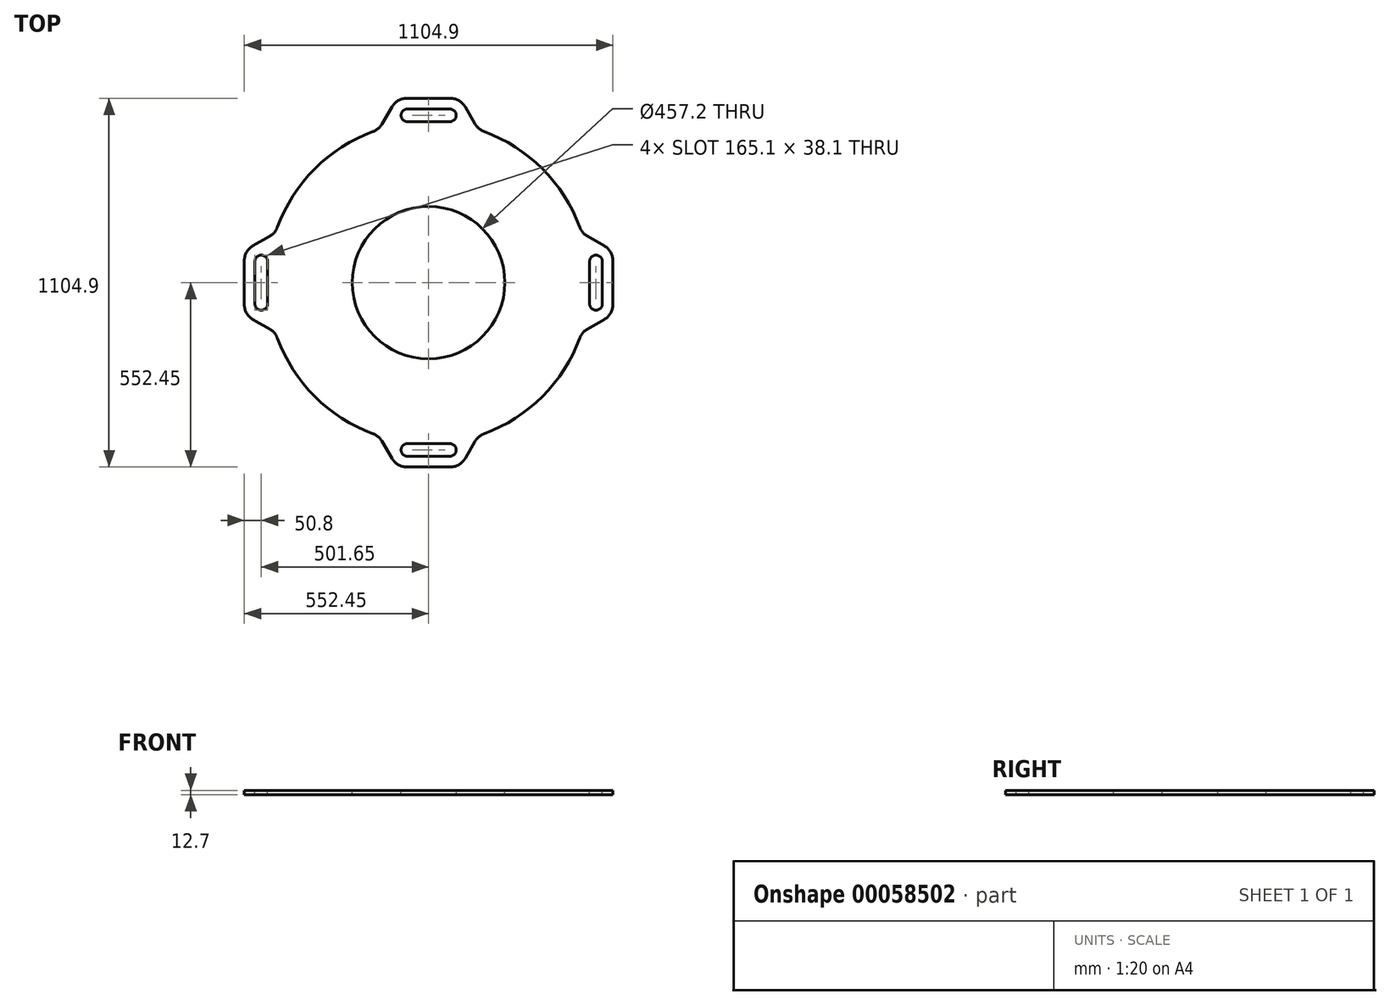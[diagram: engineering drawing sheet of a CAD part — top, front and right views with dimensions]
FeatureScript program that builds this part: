
annotation { "Feature Type Name" : "Feature", "Feature Type Description" : "" }
export const myFeature = defineFeature(function(context is Context, id is Id, definition is map)
    precondition{}
    {
        {
            var Q0;
            Q0=qCreatedBy(makeId("Top.planeOp"),FACE);
            var sketch = newSketch(context, id + "F0", { "sketchPlane" : qUnion([Q0])});
            skLineSegment(sketch, "E0.bottom", {"start": v(-552.45, 95.25) * mm, "end": v(552.45, 95.25) * mm});
            skLineSegment(sketch, "E0.top", {"start": v(-552.45, -95.25) * mm, "end": v(552.45, -95.25) * mm});
            skLineSegment(sketch, "E0.left", {"start": v(-552.45, 95.25) * mm, "end": v(-552.45, -95.25) * mm});
            skLineSegment(sketch, "E0.right", {"start": v(552.45, 95.25) * mm, "end": v(552.45, -95.25) * mm});
            skCircle(sketch, "E1", {"center": v(0, 0) * mm, "radius": 228.6 * mm});
            skCircle(sketch, "E2", {"center": v(0, 0) * mm, "radius": 482.6 * mm});
            skLineSegment(sketch, "E3.bottom", {"start": v(-95.25, 552.45) * mm, "end": v(95.25, 552.45) * mm});
            skLineSegment(sketch, "E3.top", {"start": v(-95.25, -552.45) * mm, "end": v(95.25, -552.45) * mm});
            skLineSegment(sketch, "E3.left", {"start": v(-95.25, 552.45) * mm, "end": v(-95.25, -552.45) * mm});
            skLineSegment(sketch, "E3.right", {"start": v(95.25, 552.45) * mm, "end": v(95.25, -552.45) * mm});
            skLineSegment(sketch, "E4.bottom", {"start": v(-520.7, 82.55) * mm, "end": v(-482.6, 82.55) * mm});
            skLineSegment(sketch, "E4.top", {"start": v(-520.7, -82.55) * mm, "end": v(-482.6, -82.55) * mm});
            skLineSegment(sketch, "E4.left", {"start": v(-520.7, 82.55) * mm, "end": v(-520.7, -82.55) * mm});
            skLineSegment(sketch, "E4.right", {"start": v(-482.6, 82.55) * mm, "end": v(-482.6, -82.55) * mm});
            skLineSegment(sketch, "E5", {"start": v(-552.45, 95.25) * mm, "end": v(-458.95, 149.23) * mm});
            skLineSegment(sketch, "E6", {"start": v(-552.45, -95.25) * mm, "end": v(-458.95, -149.23) * mm});
            skLineSegment(sketch, "E7", {"start": v(-95.25, 552.45) * mm, "end": v(-149.23, 458.95) * mm});
            skLineSegment(sketch, "E8", {"start": v(95.25, 552.45) * mm, "end": v(149.23, 458.95) * mm});
            skLineSegment(sketch, "E9", {"start": v(552.45, 95.25) * mm, "end": v(458.95, 149.23) * mm});
            skLineSegment(sketch, "E10", {"start": v(552.45, -95.25) * mm, "end": v(458.95, -149.23) * mm});
            skLineSegment(sketch, "E11", {"start": v(95.25, -552.45) * mm, "end": v(149.23, -458.95) * mm});
            skLineSegment(sketch, "E12", {"start": v(-95.25, -552.45) * mm, "end": v(-149.23, -458.95) * mm});
            skSolve(sketch);
        }
        {
            var Q0;
            {var subQ0=sQuery(id+"F0.wireOp",EDGE,"E0.right");Q0=makeQuery(id+"F0.imprint","IMPRINT",FACE,{"disambiguationData":[TD([[makeQuery(id+"F0.imprint","IMPRINT",EDGE,{"derivedFrom":subQ0}),-1.0]])]});}
            var Q1;
            {var subQ0=sQuery(id+"F0.wireOp",EDGE,"E2");var subQ1=sQuery(id+"F0.wireOp",EDGE,"E0.bottom");var subQ2=makeQuery(id+"F0.imprint","INTERSECT",VERTEX,{"disambiguationData":[OD(0.0)],"derivedFrom":[subQ1,subQ0]});Q1=makeQuery(id+"F0.imprint","IMPRINT",FACE,{"disambiguationData":[TD([[makeQuery(id+"F0.imprint","IMPRINT",EDGE,{"disambiguationData":[TD([[subQ2,-1.0]])],"derivedFrom":subQ1}),-1.0]])]});}
            var Q2;
            {var subQ0=sQuery(id+"F0.wireOp",EDGE,"E2");var subQ1=sQuery(id+"F0.wireOp",EDGE,"E0.bottom");var subQ2=makeQuery(id+"F0.imprint","INTERSECT",VERTEX,{"disambiguationData":[OD(1.0)],"derivedFrom":[subQ1,subQ0]});Q2=makeQuery(id+"F0.imprint","IMPRINT",FACE,{"disambiguationData":[TD([[makeQuery(id+"F0.imprint","IMPRINT",EDGE,{"disambiguationData":[TD([[subQ2,1.0]])],"derivedFrom":subQ1}),-1.0]])]});}
            var Q3;
            {var subQ0=sQuery(id+"F0.wireOp",EDGE,"E2");var subQ1=sQuery(id+"F0.wireOp",EDGE,"E0.bottom");var subQ2=makeQuery(id+"F0.imprint","INTERSECT",VERTEX,{"disambiguationData":[OD(0.0)],"derivedFrom":[subQ1,subQ0]});Q3=makeQuery(id+"F0.imprint","IMPRINT",FACE,{"disambiguationData":[TD([[makeQuery(id+"F0.imprint","IMPRINT",EDGE,{"disambiguationData":[TD([[subQ2,-1.0]])],"derivedFrom":subQ1}),1.0]])]});}
            var Q4;
            {var subQ0=sQuery(id+"F0.wireOp",EDGE,"E3.right");var subQ1=sQuery(id+"F0.wireOp",EDGE,"E1");var subQ2=makeQuery(id+"F0.imprint","INTERSECT",VERTEX,{"disambiguationData":[OD(0.0)],"derivedFrom":[subQ1,subQ0]});Q4=makeQuery(id+"F0.imprint","IMPRINT",FACE,{"disambiguationData":[TD([[makeQuery(id+"F0.imprint","IMPRINT",EDGE,{"disambiguationData":[TD([[subQ2,-1.0]])],"derivedFrom":subQ1}),-1.0]])]});}
            var Q5;
            {var subQ0=sQuery(id+"F0.wireOp",EDGE,"E2");var subQ1=sQuery(id+"F0.wireOp",EDGE,"E0.bottom");var subQ2=makeQuery(id+"F0.imprint","INTERSECT",VERTEX,{"disambiguationData":[OD(1.0)],"derivedFrom":[subQ1,subQ0]});Q5=makeQuery(id+"F0.imprint","IMPRINT",FACE,{"disambiguationData":[TD([[makeQuery(id+"F0.imprint","IMPRINT",EDGE,{"disambiguationData":[TD([[subQ2,1.0]])],"derivedFrom":subQ1}),1.0]])]});}
            var Q6;
            {var subQ5=sQuery(id+"F0.wireOp",EDGE,"E3.bottom");Q6=makeQuery(id+"F0.imprint","IMPRINT",FACE,{"disambiguationData":[TD([[makeQuery(id+"F0.imprint","IMPRINT",EDGE,{"derivedFrom":subQ5}),-1.0]])]});}
            var Q7;
            {var subQ0=sQuery(id+"F0.wireOp",EDGE,"E2");var subQ1=sQuery(id+"F0.wireOp",EDGE,"E0.top");var subQ2=makeQuery(id+"F0.imprint","INTERSECT",VERTEX,{"disambiguationData":[OD(1.0)],"derivedFrom":[subQ1,subQ0]});Q7=makeQuery(id+"F0.imprint","IMPRINT",FACE,{"disambiguationData":[TD([[makeQuery(id+"F0.imprint","IMPRINT",EDGE,{"disambiguationData":[TD([[subQ2,1.0]])],"derivedFrom":subQ1}),-1.0]])]});}
            var Q8;
            {var subQ0=sQuery(id+"F0.wireOp",EDGE,"E3.left");var subQ1=sQuery(id+"F0.wireOp",EDGE,"E1");var subQ2=makeQuery(id+"F0.imprint","INTERSECT",VERTEX,{"disambiguationData":[OD(1.0)],"derivedFrom":[subQ1,subQ0]});Q8=makeQuery(id+"F0.imprint","IMPRINT",FACE,{"disambiguationData":[TD([[makeQuery(id+"F0.imprint","IMPRINT",EDGE,{"disambiguationData":[TD([[subQ2,-1.0]])],"derivedFrom":subQ1}),-1.0]])]});}
            var Q9;
            {var subQ0=sQuery(id+"F0.wireOp",EDGE,"E2");var subQ1=sQuery(id+"F0.wireOp",EDGE,"E0.top");var subQ2=makeQuery(id+"F0.imprint","INTERSECT",VERTEX,{"disambiguationData":[OD(0.0)],"derivedFrom":[subQ1,subQ0]});Q9=makeQuery(id+"F0.imprint","IMPRINT",FACE,{"disambiguationData":[TD([[makeQuery(id+"F0.imprint","IMPRINT",EDGE,{"disambiguationData":[TD([[subQ2,-1.0]])],"derivedFrom":subQ1}),-1.0]])]});}
            var Q10;
            {var subQ5=sQuery(id+"F0.wireOp",EDGE,"E3.top");Q10=makeQuery(id+"F0.imprint","IMPRINT",FACE,{"disambiguationData":[TD([[makeQuery(id+"F0.imprint","IMPRINT",EDGE,{"derivedFrom":subQ5}),1.0]])]});}
            var Q11;
            {var subQ5=sQuery(id+"F0.wireOp",EDGE,"E0.left");Q11=makeQuery(id+"F0.imprint","IMPRINT",FACE,{"disambiguationData":[TD([[makeQuery(id+"F0.imprint","IMPRINT",EDGE,{"derivedFrom":subQ5}),1.0]])]});}
            var Q12;
            Q12=makeQuery(id+"F0.imprint","IMPRINT",FACE,{"disambiguationData":[TD([[makeQuery(id+"F0.imprint","IMPRINT",EDGE,{"derivedFrom":sQuery(id+"F0.wireOp",EDGE,"E4.bottom")}),-1.0]])]});
            var Q13;
            {var subQ0=sQuery(id+"F0.wireOp",EDGE,"E5");Q13=makeQuery(id+"F0.imprint","IMPRINT",FACE,{"disambiguationData":[TD([[makeQuery(id+"F0.imprint","IMPRINT",EDGE,{"derivedFrom":subQ0}),-1.0]])]});}
            var Q14;
            {var subQ0=sQuery(id+"F0.wireOp",EDGE,"E6");Q14=makeQuery(id+"F0.imprint","IMPRINT",FACE,{"disambiguationData":[TD([[makeQuery(id+"F0.imprint","IMPRINT",EDGE,{"derivedFrom":subQ0}),1.0]])]});}
            var Q15;
            {var subQ0=sQuery(id+"F0.wireOp",EDGE,"E7");Q15=makeQuery(id+"F0.imprint","IMPRINT",FACE,{"disambiguationData":[TD([[makeQuery(id+"F0.imprint","IMPRINT",EDGE,{"derivedFrom":subQ0}),1.0]])]});}
            var Q16;
            {var subQ0=sQuery(id+"F0.wireOp",EDGE,"E8");Q16=makeQuery(id+"F0.imprint","IMPRINT",FACE,{"disambiguationData":[TD([[makeQuery(id+"F0.imprint","IMPRINT",EDGE,{"derivedFrom":subQ0}),-1.0]])]});}
            var Q17;
            {var subQ0=sQuery(id+"F0.wireOp",EDGE,"E9");Q17=makeQuery(id+"F0.imprint","IMPRINT",FACE,{"disambiguationData":[TD([[makeQuery(id+"F0.imprint","IMPRINT",EDGE,{"derivedFrom":subQ0}),1.0]])]});}
            var Q18;
            {var subQ0=sQuery(id+"F0.wireOp",EDGE,"E10");Q18=makeQuery(id+"F0.imprint","IMPRINT",FACE,{"disambiguationData":[TD([[makeQuery(id+"F0.imprint","IMPRINT",EDGE,{"derivedFrom":subQ0}),-1.0]])]});}
            var Q19;
            {var subQ0=sQuery(id+"F0.wireOp",EDGE,"E11");Q19=makeQuery(id+"F0.imprint","IMPRINT",FACE,{"disambiguationData":[TD([[makeQuery(id+"F0.imprint","IMPRINT",EDGE,{"derivedFrom":subQ0}),1.0]])]});}
            var Q20;
            {var subQ0=sQuery(id+"F0.wireOp",EDGE,"E12");Q20=makeQuery(id+"F0.imprint","IMPRINT",FACE,{"disambiguationData":[TD([[makeQuery(id+"F0.imprint","IMPRINT",EDGE,{"derivedFrom":subQ0}),-1.0]])]});}
            extrude(context, id + "F1", {"entities" : qUnion([Q0, Q1, Q2, Q3, Q4, Q5, Q6, Q7, Q8, Q9, Q10, Q11, Q12, Q13, Q14, Q15, Q16, Q17, Q18, Q19, Q20]), "oppositeDirection" : true, "depth" : 12.7 * mm});
        }
        {
            var Q0;
            Q0=makeQuery(id+"F0.imprint","IMPRINT",FACE,{"disambiguationData":[TD([[makeQuery(id+"F0.imprint","IMPRINT",EDGE,{"derivedFrom":sQuery(id+"F0.wireOp",EDGE,"E4.bottom")}),-1.0]])]});
            extrude(context, id + "F2", {"entities" : qUnion([Q0]), "operationType" : NewBodyOperationType.REMOVE, "oppositeDirection" : true, "depth" : 25.4 * mm});
        }
        {
            var Q0;
            Q0=makeQuery(id+"F2.boolean.opBoolean","COPY",EDGE,{"derivedFrom":makeQuery(id+"F2.opExtrude","SWEPT_EDGE",EDGE,{"disambiguationData":[OSD([sQuery(id+"F0.wireOp",EDGE,"E4.top"),sQuery(id+"F0.wireOp",EDGE,"E4.left")])]})});
            var Q1;
            Q1=makeQuery(id+"F2.boolean.opBoolean","COPY",EDGE,{"derivedFrom":makeQuery(id+"F2.opExtrude","SWEPT_EDGE",EDGE,{"disambiguationData":[OSD([sQuery(id+"F0.wireOp",EDGE,"E4.top"),sQuery(id+"F0.wireOp",EDGE,"E4.right")])]})});
            var Q2;
            Q2=makeQuery(id+"F2.boolean.opBoolean","COPY",EDGE,{"derivedFrom":makeQuery(id+"F2.opExtrude","SWEPT_EDGE",EDGE,{"disambiguationData":[OSD([sQuery(id+"F0.wireOp",EDGE,"E4.bottom"),sQuery(id+"F0.wireOp",EDGE,"E4.left")])]})});
            var Q3;
            Q3=makeQuery(id+"F2.boolean.opBoolean","COPY",EDGE,{"derivedFrom":makeQuery(id+"F2.opExtrude","SWEPT_EDGE",EDGE,{"disambiguationData":[OSD([sQuery(id+"F0.wireOp",EDGE,"E4.bottom"),sQuery(id+"F0.wireOp",EDGE,"E4.right")])]})});
            fillet(context, id + "F3", {"entities" : qUnion([Q0, Q1, Q2, Q3]), "radius" : 19.05 * mm, "tangentPropagation" : true, "allowEdgeOverflow" : false});
        }
        {
            var Q0;
            Q0=makeQuery(id+"F2.boolean.opBoolean","COPY",FACE,{"derivedFrom":makeQuery(id+"F2.opExtrude","SWEPT_FACE",FACE,{"disambiguationData":[OSD([sQuery(id+"F0.wireOp",EDGE,"E4.bottom")])]})});
            var Q1;
            Q1=makeQuery(id+"F3.opFillet","BLEND_FACE",FACE,{"disambiguationData":[OSD([sQuery(id+"F0.wireOp",EDGE,"E4.bottom"),sQuery(id+"F0.wireOp",EDGE,"E4.right")])]});
            var Q2;
            Q2=makeQuery(id+"F2.boolean.opBoolean","COPY",FACE,{"derivedFrom":makeQuery(id+"F2.opExtrude","SWEPT_FACE",FACE,{"disambiguationData":[OSD([sQuery(id+"F0.wireOp",EDGE,"E4.right")])]})});
            var Q3;
            Q3=makeQuery(id+"F3.opFillet","BLEND_FACE",FACE,{"disambiguationData":[OSD([sQuery(id+"F0.wireOp",EDGE,"E4.top"),sQuery(id+"F0.wireOp",EDGE,"E4.right")])]});
            var Q4;
            Q4=makeQuery(id+"F2.boolean.opBoolean","COPY",FACE,{"derivedFrom":makeQuery(id+"F2.opExtrude","SWEPT_FACE",FACE,{"disambiguationData":[OSD([sQuery(id+"F0.wireOp",EDGE,"E4.top")])]})});
            var Q5;
            Q5=makeQuery(id+"F3.opFillet","BLEND_FACE",FACE,{"disambiguationData":[OSD([sQuery(id+"F0.wireOp",EDGE,"E4.top"),sQuery(id+"F0.wireOp",EDGE,"E4.left")])]});
            var Q6;
            Q6=makeQuery(id+"F2.boolean.opBoolean","COPY",FACE,{"derivedFrom":makeQuery(id+"F2.opExtrude","SWEPT_FACE",FACE,{"disambiguationData":[OSD([sQuery(id+"F0.wireOp",EDGE,"E4.left")])]})});
            var Q7;
            Q7=makeQuery(id+"F3.opFillet","BLEND_FACE",FACE,{"disambiguationData":[OSD([sQuery(id+"F0.wireOp",EDGE,"E4.bottom"),sQuery(id+"F0.wireOp",EDGE,"E4.left")])]});
            var Q8;
            Q8=makeQuery(id+"F1.opExtrude","SWEPT_FACE",FACE,{"disambiguationData":[OSD([sQuery(id+"F0.wireOp",EDGE,"E1")])]});
            circularPattern(context, id + "F4", {"faces" : qUnion([Q0, Q1, Q2, Q3, Q4, Q5, Q6, Q7]), "axis" : qUnion([Q8]), "angle" : 90 * degree, "instanceCount" : 4, "patternType" : PatternType.FACE});
        }
        {
            var Q0;
            Q0=makeQuery(id+"F1.opExtrude","SWEPT_EDGE",EDGE,{"disambiguationData":[OSD([sQuery(id+"F0.wireOp",EDGE,"E2"),sQuery(id+"F0.wireOp",EDGE,"E12")])]});
            var Q1;
            Q1=makeQuery(id+"F1.opExtrude","SWEPT_EDGE",EDGE,{"disambiguationData":[OSD([sQuery(id+"F0.wireOp",EDGE,"E3.top"),sQuery(id+"F0.wireOp",EDGE,"E3.left"),sQuery(id+"F0.wireOp",EDGE,"E12")])]});
            var Q2;
            Q2=makeQuery(id+"F1.opExtrude","SWEPT_EDGE",EDGE,{"disambiguationData":[OSD([sQuery(id+"F0.wireOp",EDGE,"E3.top"),sQuery(id+"F0.wireOp",EDGE,"E3.right"),sQuery(id+"F0.wireOp",EDGE,"E11")])]});
            var Q3;
            Q3=makeQuery(id+"F1.opExtrude","SWEPT_EDGE",EDGE,{"disambiguationData":[OSD([sQuery(id+"F0.wireOp",EDGE,"E2"),sQuery(id+"F0.wireOp",EDGE,"E11")])]});
            var Q4;
            Q4=makeQuery(id+"F1.opExtrude","SWEPT_EDGE",EDGE,{"disambiguationData":[OSD([sQuery(id+"F0.wireOp",EDGE,"E2"),sQuery(id+"F0.wireOp",EDGE,"E10")])]});
            var Q5;
            Q5=makeQuery(id+"F1.opExtrude","SWEPT_EDGE",EDGE,{"disambiguationData":[OSD([sQuery(id+"F0.wireOp",EDGE,"E0.top"),sQuery(id+"F0.wireOp",EDGE,"E0.right"),sQuery(id+"F0.wireOp",EDGE,"E10")])]});
            var Q6;
            Q6=makeQuery(id+"F1.opExtrude","SWEPT_EDGE",EDGE,{"disambiguationData":[OSD([sQuery(id+"F0.wireOp",EDGE,"E0.bottom"),sQuery(id+"F0.wireOp",EDGE,"E0.right"),sQuery(id+"F0.wireOp",EDGE,"E9")])]});
            var Q7;
            Q7=makeQuery(id+"F1.opExtrude","SWEPT_EDGE",EDGE,{"disambiguationData":[OSD([sQuery(id+"F0.wireOp",EDGE,"E2"),sQuery(id+"F0.wireOp",EDGE,"E9")])]});
            var Q8;
            Q8=makeQuery(id+"F1.opExtrude","SWEPT_EDGE",EDGE,{"disambiguationData":[OSD([sQuery(id+"F0.wireOp",EDGE,"E2"),sQuery(id+"F0.wireOp",EDGE,"E8")])]});
            var Q9;
            Q9=makeQuery(id+"F1.opExtrude","SWEPT_EDGE",EDGE,{"disambiguationData":[OSD([sQuery(id+"F0.wireOp",EDGE,"E3.bottom"),sQuery(id+"F0.wireOp",EDGE,"E3.right"),sQuery(id+"F0.wireOp",EDGE,"E8")])]});
            var Q10;
            Q10=makeQuery(id+"F1.opExtrude","SWEPT_EDGE",EDGE,{"disambiguationData":[OSD([sQuery(id+"F0.wireOp",EDGE,"E3.bottom"),sQuery(id+"F0.wireOp",EDGE,"E3.left"),sQuery(id+"F0.wireOp",EDGE,"E7")])]});
            var Q11;
            Q11=makeQuery(id+"F1.opExtrude","SWEPT_EDGE",EDGE,{"disambiguationData":[OSD([sQuery(id+"F0.wireOp",EDGE,"E2"),sQuery(id+"F0.wireOp",EDGE,"E7")])]});
            var Q12;
            Q12=makeQuery(id+"F1.opExtrude","SWEPT_EDGE",EDGE,{"disambiguationData":[OSD([sQuery(id+"F0.wireOp",EDGE,"E2"),sQuery(id+"F0.wireOp",EDGE,"E5")])]});
            var Q13;
            Q13=makeQuery(id+"F1.opExtrude","SWEPT_EDGE",EDGE,{"disambiguationData":[OSD([sQuery(id+"F0.wireOp",EDGE,"E0.bottom"),sQuery(id+"F0.wireOp",EDGE,"E0.left"),sQuery(id+"F0.wireOp",EDGE,"E5")])]});
            var Q14;
            Q14=makeQuery(id+"F1.opExtrude","SWEPT_EDGE",EDGE,{"disambiguationData":[OSD([sQuery(id+"F0.wireOp",EDGE,"E0.top"),sQuery(id+"F0.wireOp",EDGE,"E0.left"),sQuery(id+"F0.wireOp",EDGE,"E6")])]});
            var Q15;
            Q15=makeQuery(id+"F1.opExtrude","SWEPT_EDGE",EDGE,{"disambiguationData":[OSD([sQuery(id+"F0.wireOp",EDGE,"E2"),sQuery(id+"F0.wireOp",EDGE,"E6")])]});
            fillet(context, id + "F5", {"entities" : qUnion([Q0, Q1, Q2, Q3, Q4, Q5, Q6, Q7, Q8, Q9, Q10, Q11, Q12, Q13, Q14, Q15]), "radius" : 50.8 * mm, "tangentPropagation" : true, "allowEdgeOverflow" : false});
        }
    });
